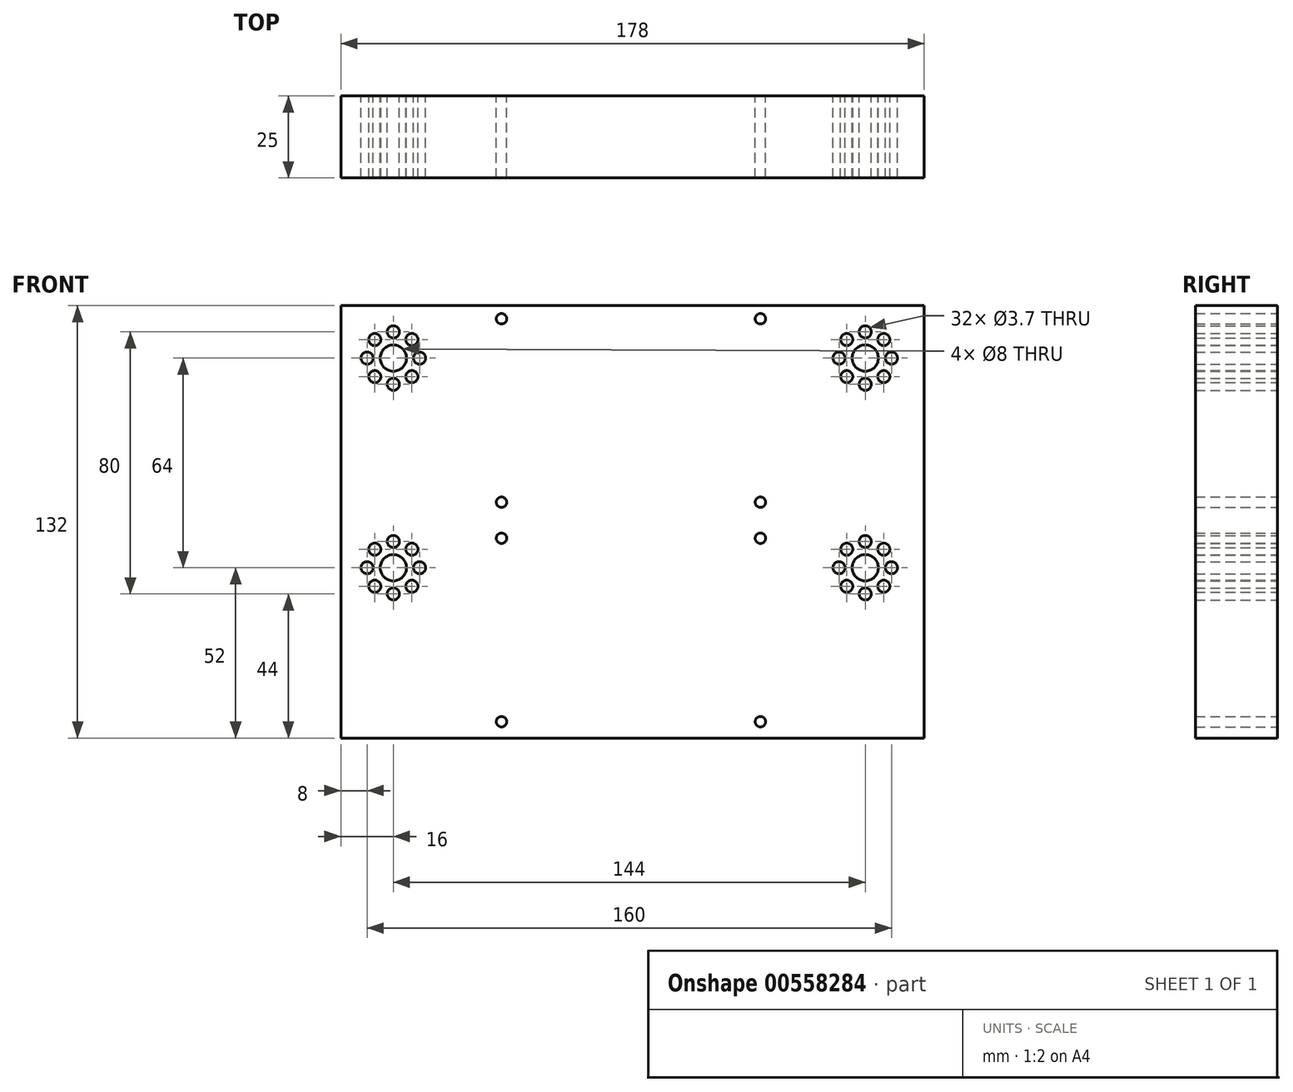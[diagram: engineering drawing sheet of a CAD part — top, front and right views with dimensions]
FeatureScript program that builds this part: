
annotation { "Feature Type Name" : "Feature", "Feature Type Description" : "" }
export const myFeature = defineFeature(function(context is Context, id is Id, definition is map)
    precondition{}
    {
        {
            var Q0;
            Q0=qCreatedBy(makeId("Front.planeOp"),FACE);
            var sketch = newSketch(context, id + "F0", { "sketchPlane" : qUnion([Q0])});
            skLineSegment(sketch, "E0.bottom", {"start": v(-89, 0) * mm, "end": v(89, 0) * mm});
            skLineSegment(sketch, "E0.top", {"start": v(-89, -132) * mm, "end": v(89, -132) * mm});
            skLineSegment(sketch, "E0.left", {"start": v(-89, 0) * mm, "end": v(-89, -132) * mm});
            skLineSegment(sketch, "E0.right", {"start": v(89, 0) * mm, "end": v(89, -132) * mm});
            skCircle(sketch, "E1", {"center": v(-73, -16) * mm, "radius": 4 * mm});
            skCircle(sketch, "E2", {"center": v(-73, -24) * mm, "radius": 1.85 * mm});
            skCircle(sketch, "E3.1.0", {"center": v(-67.34, -21.66) * mm, "radius": 1.85 * mm});
            skCircle(sketch, "E3.2.0", {"center": v(-65, -16) * mm, "radius": 1.85 * mm});
            skCircle(sketch, "E3.3.0", {"center": v(-67.34, -10.34) * mm, "radius": 1.85 * mm});
            skCircle(sketch, "E3.4.0", {"center": v(-73, -8) * mm, "radius": 1.85 * mm});
            skCircle(sketch, "E3.5.0", {"center": v(-78.66, -10.34) * mm, "radius": 1.85 * mm});
            skCircle(sketch, "E3.6.0", {"center": v(-81, -16) * mm, "radius": 1.85 * mm});
            skCircle(sketch, "E3.7.0", {"center": v(-78.66, -21.66) * mm, "radius": 1.85 * mm});
            skCircle(sketch, "E4.0.1.0", {"center": v(-73, -80) * mm, "radius": 4 * mm});
            skPoint(sketch, "E4.0.1.1", {"position": v(-73, -80) * mm});
            skCircle(sketch, "E4.0.1.2", {"center": v(-73, -88) * mm, "radius": 1.85 * mm});
            skCircle(sketch, "E4.0.1.3", {"center": v(-67.34, -85.66) * mm, "radius": 1.85 * mm});
            skCircle(sketch, "E4.0.1.4", {"center": v(-65, -80) * mm, "radius": 1.85 * mm});
            skCircle(sketch, "E4.0.1.5", {"center": v(-67.34, -74.34) * mm, "radius": 1.85 * mm});
            skCircle(sketch, "E4.0.1.6", {"center": v(-78.66, -74.34) * mm, "radius": 1.85 * mm});
            skCircle(sketch, "E4.0.1.7", {"center": v(-73, -72) * mm, "radius": 1.85 * mm});
            skCircle(sketch, "E4.0.1.8", {"center": v(-81, -80) * mm, "radius": 1.85 * mm});
            skCircle(sketch, "E4.0.1.9", {"center": v(-78.66, -85.66) * mm, "radius": 1.85 * mm});
            skCircle(sketch, "E4.1.0.0", {"center": v(71, -16) * mm, "radius": 4 * mm});
            skPoint(sketch, "E4.1.0.1", {"position": v(71, -16) * mm});
            skCircle(sketch, "E4.1.0.2", {"center": v(71, -24) * mm, "radius": 1.85 * mm});
            skCircle(sketch, "E4.1.0.3", {"center": v(76.66, -21.66) * mm, "radius": 1.85 * mm});
            skCircle(sketch, "E4.1.0.4", {"center": v(79, -16) * mm, "radius": 1.85 * mm});
            skCircle(sketch, "E4.1.0.5", {"center": v(76.66, -10.34) * mm, "radius": 1.85 * mm});
            skCircle(sketch, "E4.1.0.6", {"center": v(65.34, -10.34) * mm, "radius": 1.85 * mm});
            skCircle(sketch, "E4.1.0.7", {"center": v(71, -8) * mm, "radius": 1.85 * mm});
            skCircle(sketch, "E4.1.0.8", {"center": v(63, -16) * mm, "radius": 1.85 * mm});
            skCircle(sketch, "E4.1.0.9", {"center": v(65.34, -21.66) * mm, "radius": 1.85 * mm});
            skCircle(sketch, "E4.1.1.0", {"center": v(71, -80) * mm, "radius": 4 * mm});
            skPoint(sketch, "E4.1.1.1", {"position": v(71, -80) * mm});
            skCircle(sketch, "E4.1.1.2", {"center": v(71, -88) * mm, "radius": 1.85 * mm});
            skCircle(sketch, "E4.1.1.3", {"center": v(76.66, -85.66) * mm, "radius": 1.85 * mm});
            skCircle(sketch, "E4.1.1.4", {"center": v(79, -80) * mm, "radius": 1.85 * mm});
            skCircle(sketch, "E4.1.1.5", {"center": v(76.66, -74.34) * mm, "radius": 1.85 * mm});
            skCircle(sketch, "E4.1.1.6", {"center": v(65.34, -74.34) * mm, "radius": 1.85 * mm});
            skCircle(sketch, "E4.1.1.7", {"center": v(71, -72) * mm, "radius": 1.85 * mm});
            skCircle(sketch, "E4.1.1.8", {"center": v(63, -80) * mm, "radius": 1.85 * mm});
            skCircle(sketch, "E4.1.1.9", {"center": v(65.34, -85.66) * mm, "radius": 1.85 * mm});
            skLineSegment(sketch, "E4.direction1", {"start": v(-78.66, -21.66) * mm, "end": v(65.34, -21.66) * mm, "construction": true});
            skLineSegment(sketch, "E4.direction2", {"start": v(-78.66, -21.66) * mm, "end": v(-78.66, -85.66) * mm, "construction": true});
            skCircle(sketch, "E5", {"center": v(-40, -4) * mm, "radius": 1.6 * mm});
            skCircle(sketch, "E6", {"center": v(39, -4) * mm, "radius": 1.6 * mm});
            skCircle(sketch, "E7", {"center": v(39, -60) * mm, "radius": 1.6 * mm});
            skCircle(sketch, "E8", {"center": v(-40, -60) * mm, "radius": 1.6 * mm});
            skLineSegment(sketch, "E9.direction1", {"start": v(-81.6, -11.8) * mm, "end": v(62.4, -11.8) * mm, "construction": true});
            skCircle(sketch, "E10", {"center": v(-40, -71) * mm, "radius": 1.6 * mm});
            skCircle(sketch, "E11", {"center": v(39, -71) * mm, "radius": 1.6 * mm});
            skCircle(sketch, "E12", {"center": v(39, -127) * mm, "radius": 1.6 * mm});
            skCircle(sketch, "E13", {"center": v(-40, -127) * mm, "radius": 1.6 * mm});
            skSolve(sketch);
        }
        {
            var Q0;
            Q0=makeQuery(id+"F0.imprint","IMPRINT",FACE,{"disambiguationData":[TD([[makeQuery(id+"F0.imprint","IMPRINT",EDGE,{"derivedFrom":sQuery(id+"F0.wireOp",EDGE,"E0.bottom")}),-1.0]])]});
            extrude(context, id + "F1", {"entities" : qUnion([Q0]), "depth" : 25 * mm, "offsetDistance" : 25 * mm});
        }
    });
